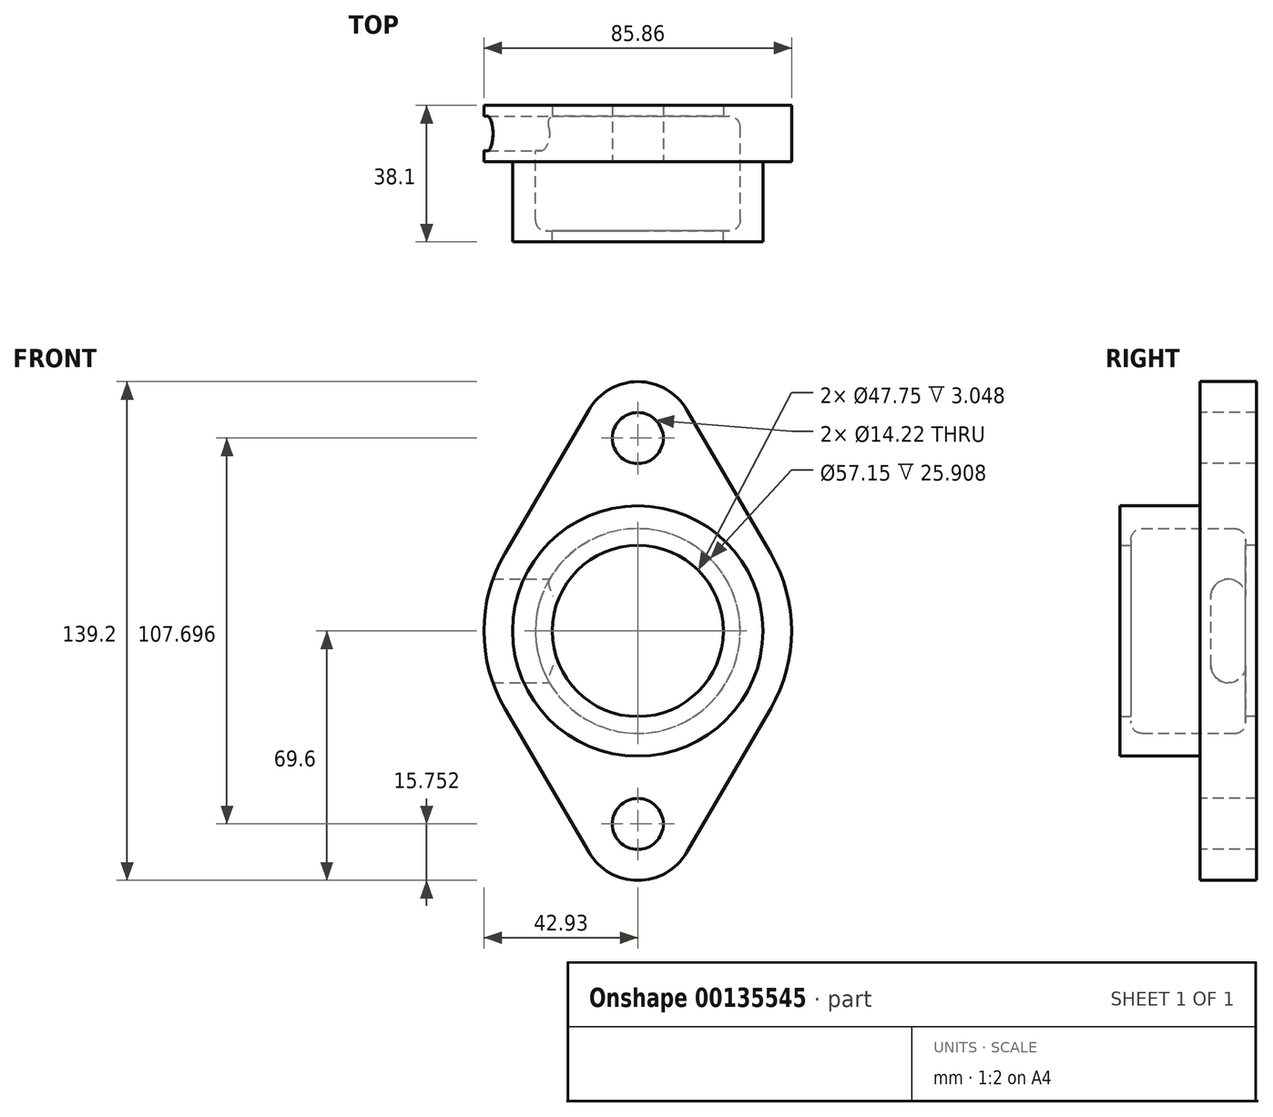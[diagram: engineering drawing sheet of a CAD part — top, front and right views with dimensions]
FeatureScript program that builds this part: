
annotation { "Feature Type Name" : "Feature", "Feature Type Description" : "" }
export const myFeature = defineFeature(function(context is Context, id is Id, definition is map)
    precondition{}
    {
        {
            var Q0;
            Q0=qCreatedBy(makeId("Front.planeOp"),FACE);
            var sketch = newSketch(context, id + "F0", { "sketchPlane" : qUnion([Q0])});
            skLineSegment(sketch, "E0", {"start": v(0, 85.06) * mm, "end": v(0, -110.68) * mm, "construction": true});
            skArc(sketch, "E1", {"start": v(-37.06, 21.67) * mm, "mid": v(-41.43, 11.22) * mm, "end": v(-42.93, 0) * mm});
            skLineSegment(sketch, "E2", {"start": v(-37.06, 21.67) * mm, "end": v(-13.6, 61.8) * mm});
            skArc(sketch, "E3", {"start": v(0, 69.6) * mm, "mid": v(-7.84, 67.5) * mm, "end": v(-13.6, 61.8) * mm});
            skLineSegment(sketch, "E4", {"start": v(-52.58, 0) * mm, "end": v(51.25, 0) * mm, "construction": true});
            skArc(sketch, "E5.MirrorCS", {"start": v(-37.06, -21.67) * mm, "mid": v(-41.43, -11.22) * mm, "end": v(-42.93, 0) * mm});
            skLineSegment(sketch, "E6.MirrorCS", {"start": v(-37.06, -21.67) * mm, "end": v(-13.6, -61.8) * mm});
            skArc(sketch, "E7.MirrorCS", {"start": v(0, -69.6) * mm, "mid": v(-7.84, -67.5) * mm, "end": v(-13.6, -61.8) * mm});
            skArc(sketch, "E8.MirrorCS", {"start": v(0, 69.6) * mm, "mid": v(7.84, 67.5) * mm, "end": v(13.6, 61.8) * mm});
            skLineSegment(sketch, "E9.MirrorCS", {"start": v(37.06, 21.67) * mm, "end": v(13.6, 61.8) * mm});
            skArc(sketch, "E10.MirrorCS", {"start": v(37.06, 21.67) * mm, "mid": v(41.43, 11.22) * mm, "end": v(42.93, 0) * mm});
            skArc(sketch, "E11.MirrorCS", {"start": v(37.06, -21.67) * mm, "mid": v(41.43, -11.22) * mm, "end": v(42.93, 0) * mm});
            skLineSegment(sketch, "E12.MirrorCS", {"start": v(37.06, -21.67) * mm, "end": v(13.6, -61.8) * mm});
            skArc(sketch, "E13.MirrorCS", {"start": v(0, -69.6) * mm, "mid": v(7.84, -67.5) * mm, "end": v(13.6, -61.8) * mm});
            skCircle(sketch, "E14", {"center": v(0, 53.85) * mm, "radius": 7.11 * mm});
            skCircle(sketch, "E15", {"center": v(0, -53.85) * mm, "radius": 7.11 * mm});
            skCircle(sketch, "E16", {"center": v(0, 0) * mm, "radius": 23.88 * mm});
            skSolve(sketch);
        }
        {
            var Q0;
            Q0 = qSketchRegion(id + "F0", true);
            extrude(context, id + "F1", {"entities" : qUnion([Q0]), "oppositeDirection" : true, "depth" : 15.75 * mm});
        }
        {
            var Q0;
            Q0=qCreatedBy(makeId("Top.planeOp"),FACE);
            var sketch = newSketch(context, id + "F2", { "sketchPlane" : qUnion([Q0])});
            skLineSegment(sketch, "E17", {"start": v(-34.92, 0) * mm, "end": v(-34.92, -22.35) * mm});
            skLineSegment(sketch, "E18", {"start": v(-34.92, -22.35) * mm, "end": v(-23.88, -22.35) * mm});
            skLineSegment(sketch, "E19", {"start": v(-23.88, -22.35) * mm, "end": v(-23.88, -19.3) * mm});
            skLineSegment(sketch, "E20", {"start": v(-23.88, -19.3) * mm, "end": v(-25.53, -19.3) * mm});
            skLineSegment(sketch, "E21", {"start": v(-28.57, -16.26) * mm, "end": v(-28.57, 0) * mm});
            skLineSegment(sketch, "E22", {"start": v(-28.57, 0) * mm, "end": v(-34.92, 0) * mm});
            skLineSegment(sketch, "E23", {"start": v(0, 65.4) * mm, "end": v(0, -89.6) * mm, "construction": true});
            skPoint(sketch, "E24.visualSharp", {"position": v(-28.57, -19.3) * mm});
            skArc(sketch, "E24.filletArc", {"start": v(-28.57, -16.26) * mm, "mid": v(-27.68, -18.41) * mm, "end": v(-25.53, -19.3) * mm});
            skSolve(sketch);
        }
        {
            var Q0;
            Q0 = qSketchRegion(id + "F2", true);
            var Q1;
            Q1=sQuery(id+"F2.wireOp",EDGE,"E23");
            revolve(context, id + "F3", {"operationType" : NewBodyOperationType.ADD, "entities" : qUnion([Q0]), "axis" : qUnion([Q1]), "revolveType" : RevolveType.FULL});
        }
        {
            var Q0;
            {var subQ0=sQuery(id+"F0.wireOp",EDGE,"E16");Q0=makeQuery(id+"F3.boolean.opBoolean","SPLIT",FACE,{"disambiguationData":[TD([makeQuery(id+"F1.opExtrude","SWEPT_FACE",FACE,{"disambiguationData":[OSD([subQ0])]})])],"derivedFrom":makeQuery(id+"F1.opExtrude","CAP_FACE",FACE,{"disambiguationData":[OSD([sQuery(id+"F0.wireOp",EDGE,"E1"),sQuery(id+"F0.wireOp",EDGE,"E2"),sQuery(id+"F0.wireOp",EDGE,"E3"),sQuery(id+"F0.wireOp",EDGE,"E5.MirrorCS"),sQuery(id+"F0.wireOp",EDGE,"E6.MirrorCS"),sQuery(id+"F0.wireOp",EDGE,"E7.MirrorCS"),sQuery(id+"F0.wireOp",EDGE,"E8.MirrorCS"),sQuery(id+"F0.wireOp",EDGE,"E9.MirrorCS"),sQuery(id+"F0.wireOp",EDGE,"E10.MirrorCS"),sQuery(id+"F0.wireOp",EDGE,"E11.MirrorCS"),sQuery(id+"F0.wireOp",EDGE,"E12.MirrorCS"),sQuery(id+"F0.wireOp",EDGE,"E13.MirrorCS"),sQuery(id+"F0.wireOp",EDGE,"E14"),sQuery(id+"F0.wireOp",EDGE,"E15"),subQ0])],"isStart":true})});}
            var sketch = newSketch(context, id + "F4", { "sketchPlane" : qUnion([Q0])});
            skCircle(sketch, "E25", {"center": v(0, 0) * mm, "radius": 28.58 * mm});
            skSolve(sketch);
        }
        {
            var Q0;
            Q0 = qSketchRegion(id + "F4", true);
            extrude(context, id + "F5", {"entities" : qUnion([Q0]), "operationType" : NewBodyOperationType.REMOVE, "oppositeDirection" : true, "depth" : 12.7 * mm});
        }
        {
            var Q0;
            Q0=makeQuery(id+"F5.boolean.opBoolean","COPY",EDGE,{"derivedFrom":makeQuery(id+"F5.opExtrude","CAP_EDGE",EDGE,{"disambiguationData":[OSD([sQuery(id+"F4.wireOp",EDGE,"E25")])],"isStart":false})});
            fillet(context, id + "F6", {"entities" : qUnion([Q0]), "radius" : 3.05 * mm, "tangentPropagation" : true, "allowEdgeOverflow" : false});
        }
        {
            var Q0;
            Q0=qCreatedBy(makeId("Right.planeOp"),FACE);
            var sketch = newSketch(context, id + "F7", { "sketchPlane" : qUnion([Q0])});
            skLineSegment(sketch, "E26", {"start": v(3.05, 0) * mm, "end": v(3.05, 9.65) * mm});
            skArc(sketch, "E27", {"start": v(12.7, 9.65) * mm, "mid": v(7.87, 14.48) * mm, "end": v(3.05, 9.65) * mm});
            skLineSegment(sketch, "E28", {"start": v(12.7, 9.65) * mm, "end": v(12.7, 0) * mm});
            skLineSegment(sketch, "E29", {"start": v(0, 0) * mm, "end": v(52.65, 0) * mm, "construction": true});
            skLineSegment(sketch, "E30.MirrorCS", {"start": v(12.7, -9.65) * mm, "end": v(12.7, 0) * mm});
            skLineSegment(sketch, "E31.MirrorCS", {"start": v(3.05, 0) * mm, "end": v(3.05, -9.65) * mm});
            skArc(sketch, "E32.MirrorCS", {"start": v(12.7, -9.65) * mm, "mid": v(7.87, -14.48) * mm, "end": v(3.05, -9.65) * mm});
            skSolve(sketch);
        }
        {
            var Q0;
            Q0 = qSketchRegion(id + "F7", true);
            extrude(context, id + "F8", {"entities" : qUnion([Q0]), "operationType" : NewBodyOperationType.REMOVE, "endBound" : BoundingType.THROUGH_ALL, "oppositeDirection" : true, "depth" : 25.4 * mm});
        }
    });
